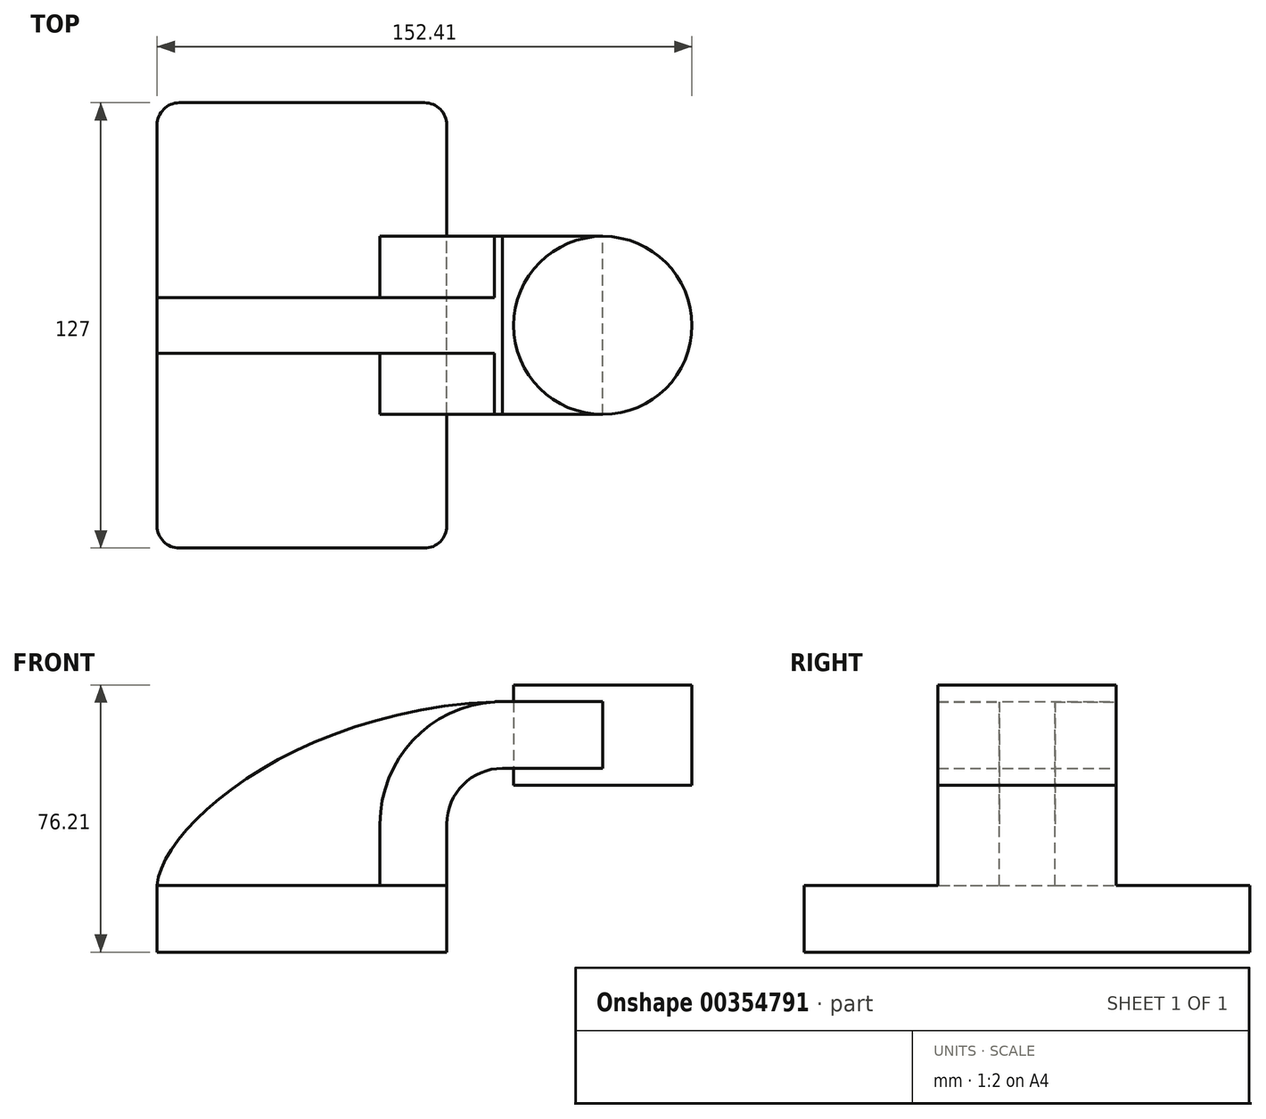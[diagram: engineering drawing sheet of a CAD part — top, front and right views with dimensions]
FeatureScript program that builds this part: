
annotation { "Feature Type Name" : "Feature", "Feature Type Description" : "" }
export const myFeature = defineFeature(function(context is Context, id is Id, definition is map)
    precondition{}
    {
        {
            var Q0;
            Q0=qCreatedBy(makeId("Front.planeOp"),FACE);
            var sketch = newSketch(context, id + "F0", { "sketchPlane" : qUnion([Q0])});
            skLineSegment(sketch, "E0.bottom", {"start": v(41.28, -9.52) * mm, "end": v(-41.28, -9.53) * mm});
            skLineSegment(sketch, "E0.top", {"start": v(41.28, 9.53) * mm, "end": v(-41.28, 9.53) * mm});
            skLineSegment(sketch, "E0.left", {"start": v(41.28, -9.52) * mm, "end": v(41.28, 9.53) * mm});
            skLineSegment(sketch, "E0.right", {"start": v(-41.28, -9.53) * mm, "end": v(-41.28, 9.53) * mm});
            skPoint(sketch, "E0.middle", {"position": v(0, 0) * mm});
            skLineSegment(sketch, "E1.bottom", {"start": v(60.33, 38.1) * mm, "end": v(111.13, 38.1) * mm});
            skLineSegment(sketch, "E1.top", {"start": v(60.32, 66.68) * mm, "end": v(111.12, 66.68) * mm});
            skLineSegment(sketch, "E1.left", {"start": v(60.33, 38.1) * mm, "end": v(60.32, 66.68) * mm});
            skLineSegment(sketch, "E1.right", {"start": v(111.13, 38.1) * mm, "end": v(111.12, 66.68) * mm});
            skPoint(sketch, "E1.middle", {"position": v(85.72, 52.39) * mm});
            skLineSegment(sketch, "E2", {"start": v(41.28, 9.53) * mm, "end": v(41.28, 27) * mm});
            skArc(sketch, "E3", {"start": v(41.27, 27) * mm, "mid": v(45.92, 38.23) * mm, "end": v(57.15, 42.88) * mm});
            skLineSegment(sketch, "E4", {"start": v(57.15, 42.88) * mm, "end": v(85.72, 42.88) * mm});
            skPoint(sketch, "E4.endSnap0", {"position": v(85.73, 38.1) * mm});
            skLineSegment(sketch, "E5.0", {"start": v(57.15, 61.93) * mm, "end": v(85.72, 61.93) * mm});
            skArc(sketch, "E5.1", {"start": v(22.23, 27) * mm, "mid": v(32.45, 51.7) * mm, "end": v(57.15, 61.93) * mm});
            skLineSegment(sketch, "E5.2", {"start": v(22.22, 9.53) * mm, "end": v(22.22, 27) * mm});
            skLineSegment(sketch, "E6", {"start": v(85.72, 38.1) * mm, "end": v(85.72, 66.68) * mm});
            skFitSpline(sketch, "E7", {"points": [v(-41.28, 9.53) * mm, v(57.15, 61.93) * mm], "startDerivative": vector(4.35, 52.4) * mm, "endDerivative": vector(171.45, 4.35) * mm});
            skSolve(sketch);
        }
        {
            var Q0;
            Q0=makeQuery(id+"F0.imprint","IMPRINT",FACE,{"disambiguationData":[TD([[makeQuery(id+"F0.imprint","IMPRINT",EDGE,{"derivedFrom":sQuery(id+"F0.wireOp",EDGE,"E0.bottom")}),-1.0]])]});
            extrude(context, id + "F1", {"entities" : qUnion([Q0]), "endBound" : BoundingType.SYMMETRIC, "depth" : 127 * mm});
        }
        {
            var Q0;
            {var subQ1=sQuery(id+"F0.wireOp",EDGE,"E2");Q0=makeQuery(id+"F0.imprint","IMPRINT",FACE,{"disambiguationData":[TD([[makeQuery(id+"F0.imprint","IMPRINT",EDGE,{"derivedFrom":subQ1}),1.0]])]});}
            var Q1;
            {var subQ0=sQuery(id+"F0.wireOp",EDGE,"E4");var subQ1=sQuery(id+"F0.wireOp",EDGE,"E1.left");var subQ2=makeQuery(id+"F0.imprint","INTERSECT",VERTEX,{"derivedFrom":[subQ1,subQ0]});Q1=makeQuery(id+"F0.imprint","IMPRINT",FACE,{"disambiguationData":[TD([[makeQuery(id+"F0.imprint","IMPRINT",EDGE,{"disambiguationData":[TD([[subQ2,-1.0]])],"derivedFrom":subQ1}),-1.0]])]});}
            extrude(context, id + "F2", {"entities" : qUnion([Q0, Q1]), "operationType" : NewBodyOperationType.ADD, "endBound" : BoundingType.SYMMETRIC, "depth" : 50.8 * mm});
        }
        {
            var Q0;
            {var subQ3=sQuery(id+"F0.wireOp",EDGE,"E5.2");Q0=makeQuery(id+"F0.imprint","IMPRINT",FACE,{"disambiguationData":[TD([[makeQuery(id+"F0.imprint","IMPRINT",EDGE,{"derivedFrom":subQ3}),1.0]])]});}
            extrude(context, id + "F3", {"entities" : qUnion([Q0]), "operationType" : NewBodyOperationType.ADD, "endBound" : BoundingType.SYMMETRIC, "depth" : 15.88 * mm});
        }
        {
            var Q0;
            {var subQ4=sQuery(id+"F0.wireOp",EDGE,"E1.right");Q0=makeQuery(id+"F0.imprint","IMPRINT",FACE,{"disambiguationData":[TD([[makeQuery(id+"F0.imprint","IMPRINT",EDGE,{"derivedFrom":subQ4}),1.0]])]});}
            var Q1;
            Q1=sQuery(id+"F0.wireOp",EDGE,"E6");
            revolve(context, id + "F4", {"entities" : qUnion([Q0]), "axis" : qUnion([Q1]), "revolveType" : RevolveType.FULL});
        }
        {
            var Q0;
            Q0=makeQuery(id+"F1.opExtrude","CAP_EDGE",EDGE,{"disambiguationData":[OSD([sQuery(id+"F0.wireOp",EDGE,"E0.left")])],"isStart":false});
            var Q1;
            Q1=makeQuery(id+"F1.opExtrude","CAP_EDGE",EDGE,{"disambiguationData":[OSD([sQuery(id+"F0.wireOp",EDGE,"E0.right")])],"isStart":false});
            var Q2;
            Q2=makeQuery(id+"F1.opExtrude","CAP_EDGE",EDGE,{"disambiguationData":[OSD([sQuery(id+"F0.wireOp",EDGE,"E0.left")])],"isStart":true});
            var Q3;
            Q3=makeQuery(id+"F1.opExtrude","CAP_EDGE",EDGE,{"disambiguationData":[OSD([sQuery(id+"F0.wireOp",EDGE,"E0.right")])],"isStart":true});
            fillet(context, id + "F5", {"entities" : qUnion([Q0, Q1, Q2, Q3]), "radius" : 6.35 * mm, "tangentPropagation" : true, "allowEdgeOverflow" : false});
        }
    });
